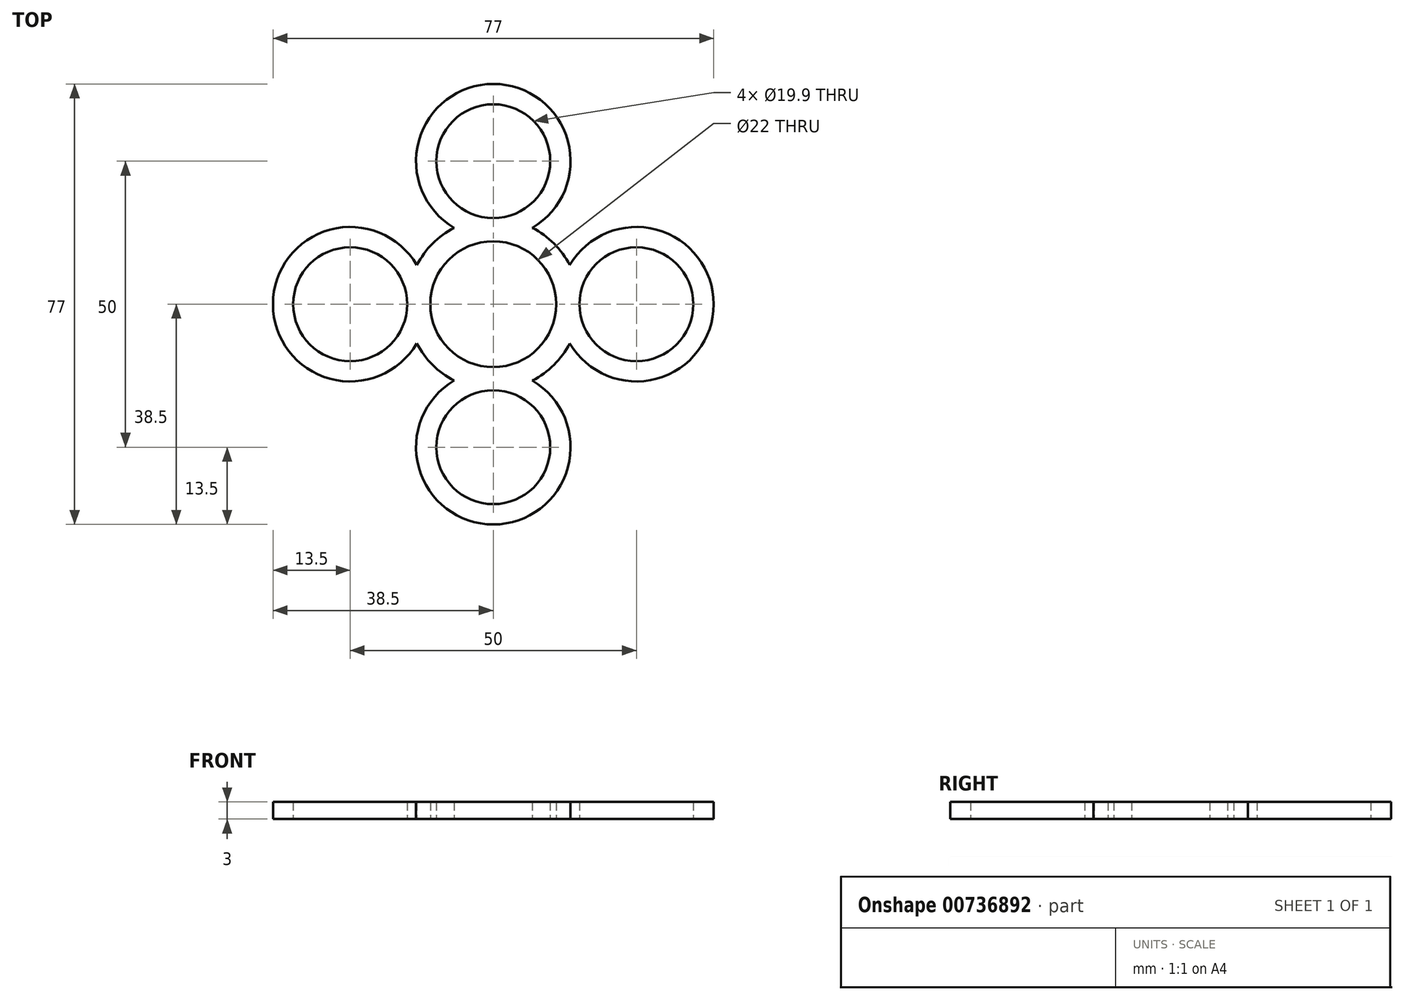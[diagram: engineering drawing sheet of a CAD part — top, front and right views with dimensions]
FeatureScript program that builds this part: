
annotation { "Feature Type Name" : "Feature", "Feature Type Description" : "" }
export const myFeature = defineFeature(function(context is Context, id is Id, definition is map)
    precondition{}
    {
        {
            var Q0;
            Q0=qCreatedBy(makeId("Top.planeOp"),FACE);
            var sketch = newSketch(context, id + "F0", { "sketchPlane" : qUnion([Q0])});
            skArc(sketch, "E0", {"start": v(7.78, 7.78) * mm, "mid": v(0, 11) * mm, "end": v(-7.78, 7.78) * mm});
            skCircle(sketch, "E1", {"center": v(0, 25) * mm, "radius": 9.95 * mm});
            skArc(sketch, "E2", {"start": v(-6.83, 13.35) * mm, "mid": v(-8.83, 12.13) * mm, "end": v(-10.6, 10.6) * mm});
            skArc(sketch, "E3", {"start": v(6.83, 13.36) * mm, "mid": v(0, 38.5) * mm, "end": v(-6.83, 13.36) * mm});
            skArc(sketch, "E4.trimOffspring", {"start": v(10.6, 10.6) * mm, "mid": v(8.83, 12.13) * mm, "end": v(6.83, 13.36) * mm});
            skCircle(sketch, "E5.1.0", {"center": v(-25, 0) * mm, "radius": 9.95 * mm});
            skArc(sketch, "E5.1.1", {"start": v(-13.36, 6.83) * mm, "mid": v(-38.5, 0) * mm, "end": v(-13.36, -6.83) * mm});
            skArc(sketch, "E5.1.2", {"start": v(-7.78, 7.78) * mm, "mid": v(-11, 0) * mm, "end": v(-7.78, -7.78) * mm});
            skArc(sketch, "E5.1.3", {"start": v(-13.35, -6.83) * mm, "mid": v(-12.13, -8.83) * mm, "end": v(-10.6, -10.6) * mm});
            skArc(sketch, "E5.1.4", {"start": v(-10.6, 10.6) * mm, "mid": v(-12.13, 8.83) * mm, "end": v(-13.36, 6.83) * mm});
            skCircle(sketch, "E5.2.0", {"center": v(0, -25) * mm, "radius": 9.95 * mm});
            skArc(sketch, "E5.2.1", {"start": v(-6.83, -13.35) * mm, "mid": v(0, -38.5) * mm, "end": v(6.83, -13.36) * mm});
            skArc(sketch, "E5.2.2", {"start": v(-7.78, -7.78) * mm, "mid": v(0, -11) * mm, "end": v(7.78, -7.78) * mm});
            skArc(sketch, "E5.2.3", {"start": v(6.83, -13.35) * mm, "mid": v(8.83, -12.13) * mm, "end": v(10.6, -10.6) * mm});
            skArc(sketch, "E5.2.4", {"start": v(-10.6, -10.6) * mm, "mid": v(-8.83, -12.13) * mm, "end": v(-6.83, -13.35) * mm});
            skCircle(sketch, "E5.3.0", {"center": v(25, 0) * mm, "radius": 9.95 * mm});
            skArc(sketch, "E5.3.1", {"start": v(13.35, -6.83) * mm, "mid": v(38.5, 0) * mm, "end": v(13.36, 6.83) * mm});
            skArc(sketch, "E5.3.2", {"start": v(7.78, -7.78) * mm, "mid": v(11, 0) * mm, "end": v(7.78, 7.78) * mm});
            skArc(sketch, "E5.3.3", {"start": v(13.35, 6.83) * mm, "mid": v(12.13, 8.83) * mm, "end": v(10.6, 10.6) * mm});
            skArc(sketch, "E5.3.4", {"start": v(10.6, -10.6) * mm, "mid": v(12.13, -8.83) * mm, "end": v(13.35, -6.83) * mm});
            skSolve(sketch);
        }
        {
            var Q0;
            Q0 = qSketchRegion(id + "F0", true);
            extrude(context, id + "F1", {"entities" : qUnion([Q0]), "depth" : 3 * mm, "offsetDistance" : 25 * mm});
        }
    });
